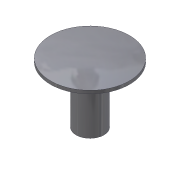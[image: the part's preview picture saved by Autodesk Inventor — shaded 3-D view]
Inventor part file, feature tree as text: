
AUTODESK INVENTOR PART (.ipt)
format: ipt  version: 2016 SP1 (Build 200210100, 210)  size: 92,672 bytes
history: native  units: mm (DEFAULTED — no unit token found)
features: sketch x2, reference x2, revolve x1, extrude x1
ambient origin geometry x8: Origin, YZ Plane, XZ Plane, XY Plane, X Axis, Y Axis, Z Axis, Center Point
bodies: Solid1 (feature_tree)
feature tree (6):
  revolve  "Revolution1"  [1 undecoded]
  extrude  "Extrusion1"  [1 undecoded]
  sketch  "Sketch1"  dims[d0=90.0deg d1=3.175mm d2=0.0mm]
  reference  "Reference1"
  reference  "Reference2"
  sketch  "Sketch2"
note: 2 required parameter values undecoded (feature->parameter linkage not recoverable at this tier; creation-order binding heuristic only, values carry confidence <= 0.55)